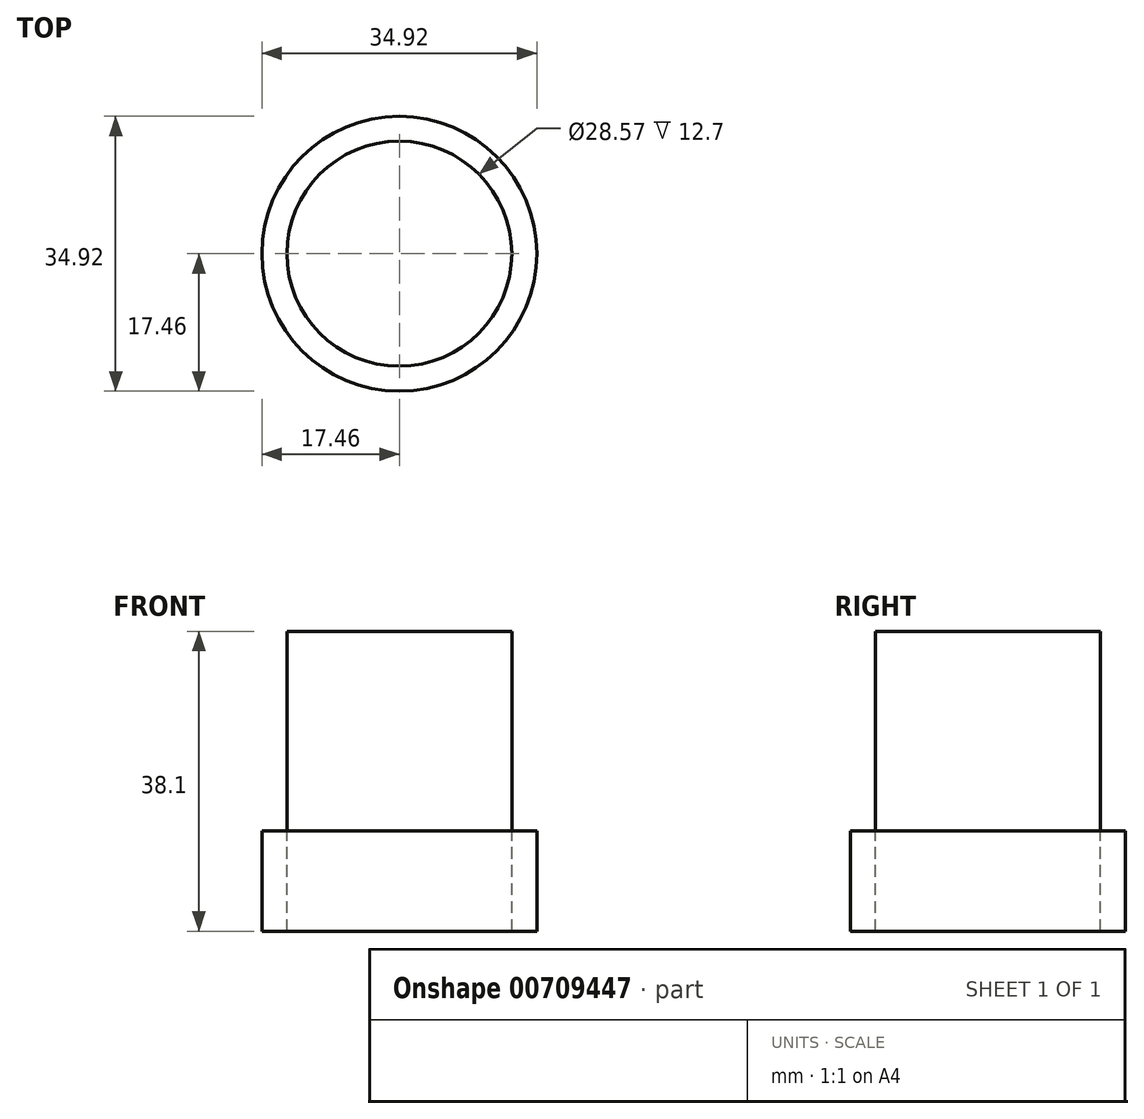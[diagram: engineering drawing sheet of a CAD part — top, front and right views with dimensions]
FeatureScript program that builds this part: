
annotation { "Feature Type Name" : "Feature", "Feature Type Description" : "" }
export const myFeature = defineFeature(function(context is Context, id is Id, definition is map)
    precondition{}
    {
        {
            var Q0;
            Q0=qCreatedBy(makeId("Top.planeOp"),FACE);
            var sketch = newSketch(context, id + "F0", { "sketchPlane" : qUnion([Q0])});
            skCircle(sketch, "E0", {"center": v(0, 0) * mm, "radius": 14.29 * mm});
            skCircle(sketch, "E1.0", {"center": v(0, 0) * mm, "radius": 17.46 * mm});
            skSolve(sketch);
        }
        {
            var Q0;
            Q0=makeQuery(id+"F0.imprint","IMPRINT",FACE,{"disambiguationData":[TD([[makeQuery(id+"F0.imprint","IMPRINT",EDGE,{"derivedFrom":sQuery(id+"F0.wireOp",EDGE,"E0")}),1.0]])]});
            extrude(context, id + "F1", {"entities" : qUnion([Q0]), "depth" : 25.4 * mm, "offsetDistance" : 25.4 * mm});
        }
        {
            var Q0;
            Q0=qSketchRegion(id+"F0",true);
            extrude(context, id + "F2", {"entities" : qUnion([Q0]), "operationType" : NewBodyOperationType.ADD, "oppositeDirection" : true, "depth" : 12.7 * mm, "offsetDistance" : 25.4 * mm, "hasSecondDirection" : true, "secondDirectionOppositeDirection" : false, "secondDirectionDepth" : 0.03 * mm});
        }
    });
